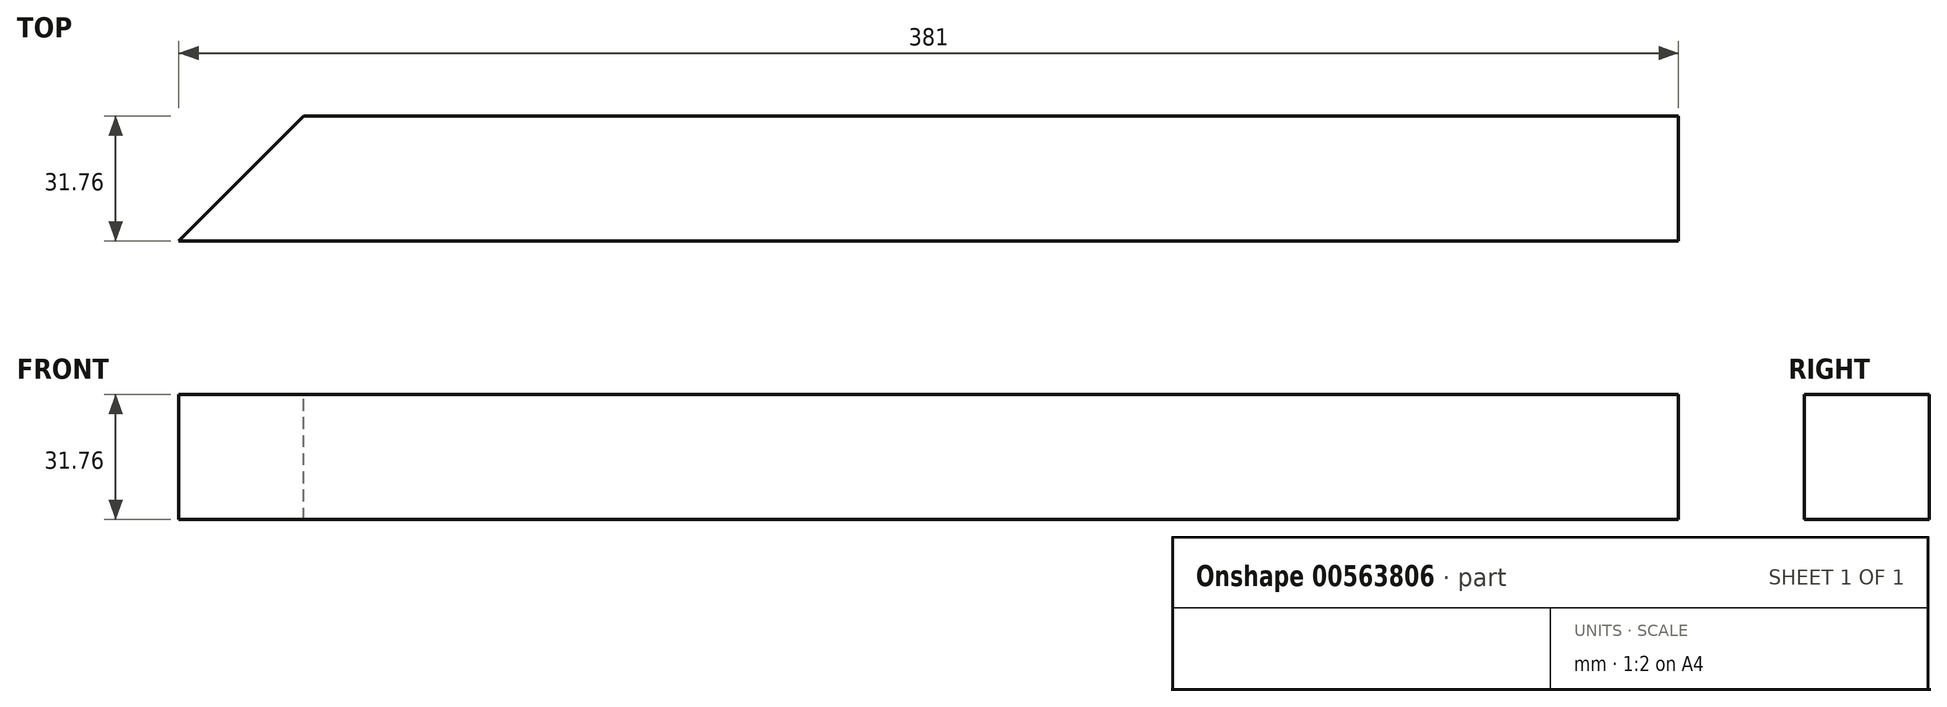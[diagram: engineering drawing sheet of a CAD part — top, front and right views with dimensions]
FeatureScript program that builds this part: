
annotation { "Feature Type Name" : "Feature", "Feature Type Description" : "" }
export const myFeature = defineFeature(function(context is Context, id is Id, definition is map)
    precondition{}
    {
        {
            var Q0;
            Q0=qCreatedBy(makeId("Top.planeOp"),FACE);
            var sketch = newSketch(context, id + "F0", { "sketchPlane" : qUnion([Q0])});
            skLineSegment(sketch, "E0.bottom", {"start": v(-190.5, 15.88) * mm, "end": v(190.5, 15.88) * mm});
            skLineSegment(sketch, "E0.top", {"start": v(-190.5, -15.87) * mm, "end": v(190.5, -15.87) * mm});
            skLineSegment(sketch, "E0.left", {"start": v(-190.5, 15.88) * mm, "end": v(-190.5, -15.87) * mm});
            skLineSegment(sketch, "E0.right", {"start": v(190.5, 15.88) * mm, "end": v(190.5, -15.87) * mm});
            skPoint(sketch, "E0.middle", {"position": v(0, 0) * mm});
            skSolve(sketch);
        }
        {
            var Q0;
            Q0=makeQuery(id+"F0.imprint","IMPRINT",FACE,{"disambiguationData":[TD([[makeQuery(id+"F0.imprint","IMPRINT",EDGE,{"derivedFrom":sQuery(id+"F0.wireOp",EDGE,"E0.bottom")}),-1.0]])]});
            extrude(context, id + "F1", {"entities" : qUnion([Q0]), "endBound" : BoundingType.SYMMETRIC, "depth" : 31.75 * mm, "offsetDistance" : 25.4 * mm});
        }
        {
            var Q0;
            Q0=makeQuery(id+"F1.opExtrude","CAP_FACE",FACE,{"disambiguationData":[OSD([sQuery(id+"F0.wireOp",EDGE,"E0.bottom"),sQuery(id+"F0.wireOp",EDGE,"E0.top"),sQuery(id+"F0.wireOp",EDGE,"E0.left"),sQuery(id+"F0.wireOp",EDGE,"E0.right")])],"isStart":false});
            var sketch = newSketch(context, id + "F2", { "sketchPlane" : qUnion([Q0])});
            skLineSegment(sketch, "E1", {"start": v(-190.5, -15.87) * mm, "end": v(-158.75, 15.88) * mm});
            skSolve(sketch);
        }
        {
            var Q0;
            {var subQ0=sQuery(id+"F2.wireOp",EDGE,"E1");Q0=makeQuery(id+"F2.imprint","IMPRINT",FACE,{"disambiguationData":[TD([[makeQuery(id+"F2.imprint","IMPRINT",EDGE,{"derivedFrom":subQ0}),1.0]])]});}
            extrude(context, id + "F3", {"entities" : qUnion([Q0]), "operationType" : NewBodyOperationType.REMOVE, "oppositeDirection" : true, "depth" : 31.75 * mm, "offsetDistance" : 25.4 * mm});
        }
    });
